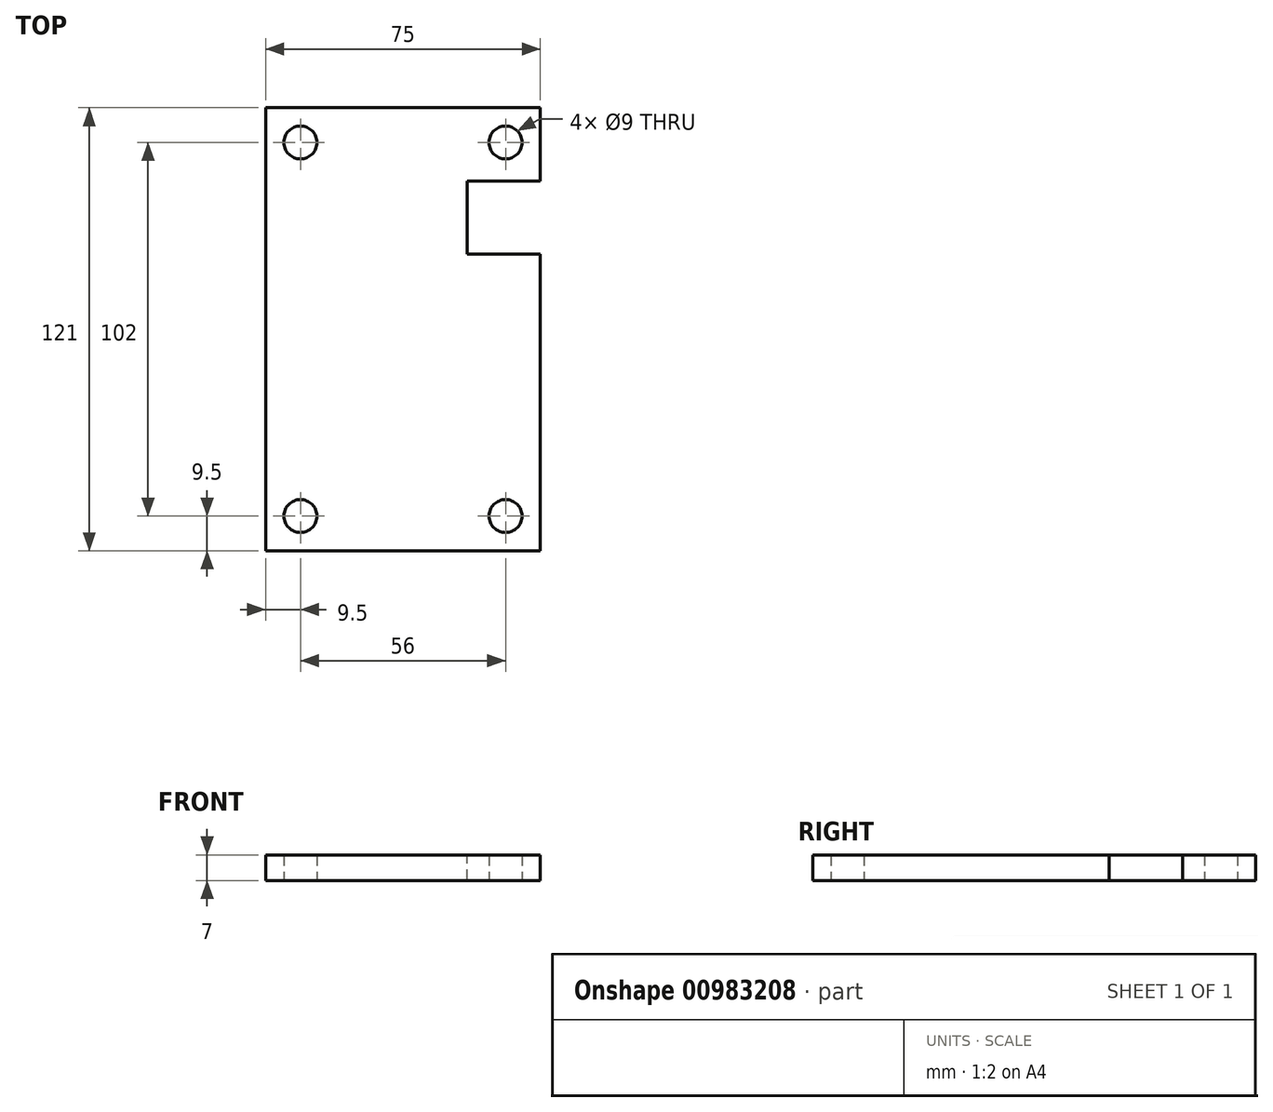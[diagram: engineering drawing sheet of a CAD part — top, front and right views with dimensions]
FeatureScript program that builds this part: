
annotation { "Feature Type Name" : "Feature", "Feature Type Description" : "" }
export const myFeature = defineFeature(function(context is Context, id is Id, definition is map)
    precondition{}
    {
        {
            var Q0;
            Q0=qCreatedBy(makeId("Top.planeOp"),FACE);
            var sketch = newSketch(context, id + "F0", { "sketchPlane" : qUnion([Q0])});
            skLineSegment(sketch, "E0.bottom", {"start": v(-37.5, -60.5) * mm, "end": v(37.5, -60.5) * mm});
            skLineSegment(sketch, "E0.top", {"start": v(-37.5, 60.5) * mm, "end": v(37.5, 60.5) * mm});
            skLineSegment(sketch, "E0.left", {"start": v(-37.5, -60.5) * mm, "end": v(-37.5, 60.5) * mm});
            skLineSegment(sketch, "E0.right", {"start": v(37.5, -60.5) * mm, "end": v(37.5, 60.5) * mm});
            skPoint(sketch, "E0.middle", {"position": v(0, 0) * mm});
            skLineSegment(sketch, "E1.bottom", {"start": v(28, -51) * mm, "end": v(-28, -51) * mm});
            skLineSegment(sketch, "E1.top", {"start": v(28, 51) * mm, "end": v(-28, 51) * mm});
            skLineSegment(sketch, "E1.left", {"start": v(28, -51) * mm, "end": v(28, 51) * mm});
            skLineSegment(sketch, "E1.right", {"start": v(-28, -51) * mm, "end": v(-28, 51) * mm});
            skCircle(sketch, "E2", {"center": v(-28, 51) * mm, "radius": 4.5 * mm});
            skCircle(sketch, "E3", {"center": v(-28, -51) * mm, "radius": 4.5 * mm});
            skCircle(sketch, "E4", {"center": v(28, -51) * mm, "radius": 4.5 * mm});
            skCircle(sketch, "E5", {"center": v(28, 51) * mm, "radius": 4.5 * mm});
            skSolve(sketch);
        }
        {
            var Q0;
            Q0=makeQuery(id+"F0.imprint","IMPRINT",FACE,{"disambiguationData":[TD([[makeQuery(id+"F0.imprint","IMPRINT",EDGE,{"derivedFrom":sQuery(id+"F0.wireOp",EDGE,"E0.bottom")}),1.0]])]});
            var Q1;
            {var subQ5=sQuery(id+"F0.wireOp",EDGE,"E4");var subQ13=sQuery(id+"F0.wireOp",EDGE,"E1.bottom");var subQ14=makeQuery(id+"F0.imprint","INTERSECT",VERTEX,{"derivedFrom":[subQ13,subQ5]});Q1=makeQuery(id+"F0.imprint","IMPRINT",FACE,{"disambiguationData":[TD([[makeQuery(id+"F0.imprint","IMPRINT",EDGE,{"disambiguationData":[TD([[subQ14,-1.0]])],"derivedFrom":subQ13}),-1.0]])]});}
            extrude(context, id + "F1", {"entities" : qUnion([Q0, Q1]), "depth" : 7 * mm, "offsetDistance" : 25 * mm});
        }
        {
            var Q0;
            Q0=makeQuery(id+"F1.opExtrude","CAP_FACE",FACE,{"disambiguationData":[OSD([sQuery(id+"F0.wireOp",EDGE,"E0.bottom"),sQuery(id+"F0.wireOp",EDGE,"E0.top"),sQuery(id+"F0.wireOp",EDGE,"E0.left"),sQuery(id+"F0.wireOp",EDGE,"E0.right"),sQuery(id+"F0.wireOp",EDGE,"E2"),sQuery(id+"F0.wireOp",EDGE,"E3"),sQuery(id+"F0.wireOp",EDGE,"E4"),sQuery(id+"F0.wireOp",EDGE,"E5")])],"isStart":false});
            var sketch = newSketch(context, id + "F2", { "sketchPlane" : qUnion([Q0])});
            skLineSegment(sketch, "E6.bottom", {"start": v(37.5, 40.5) * mm, "end": v(17.5, 40.5) * mm});
            skLineSegment(sketch, "E6.top", {"start": v(37.5, 20.5) * mm, "end": v(17.5, 20.5) * mm});
            skLineSegment(sketch, "E6.left", {"start": v(37.5, 40.5) * mm, "end": v(37.5, 20.5) * mm});
            skLineSegment(sketch, "E6.right", {"start": v(17.5, 40.5) * mm, "end": v(17.5, 20.5) * mm});
            skSolve(sketch);
        }
        {
            var Q0;
            Q0=makeQuery(id+"F2.imprint","IMPRINT",FACE,{"disambiguationData":[TD([[makeQuery(id+"F2.imprint","IMPRINT",EDGE,{"derivedFrom":sQuery(id+"F2.wireOp",EDGE,"E6.bottom")}),1.0]])]});
            var Q1;
            Q1=sQuery(id+"F2.wireOp",EDGE,"E6.top");
            var Q2;
            Q2=sQuery(id+"F2.wireOp",EDGE,"E6.right");
            var Q3;
            Q3=sQuery(id+"F2.wireOp",EDGE,"E6.bottom");
            var Q4;
            Q4=sQuery(id+"F2.wireOp",EDGE,"E6.left");
            extrude(context, id + "F3", {"entities" : qUnion([Q0]), "operationType" : NewBodyOperationType.REMOVE, "surfaceEntities" : qUnion([Q1, Q2, Q3, Q4]), "oppositeDirection" : true, "depth" : 25 * mm, "offsetDistance" : 25 * mm});
        }
    });
